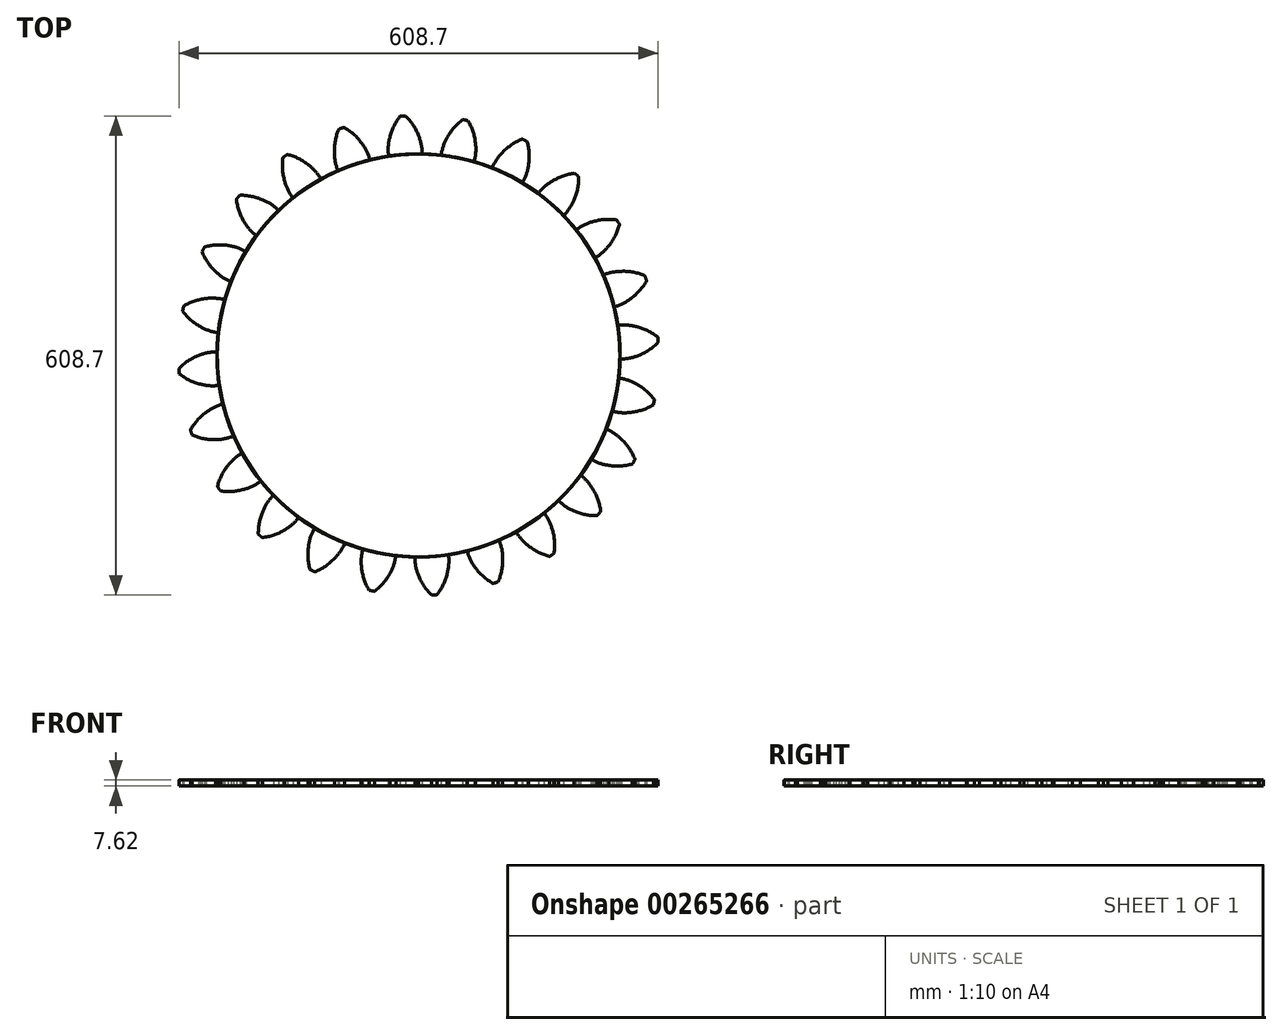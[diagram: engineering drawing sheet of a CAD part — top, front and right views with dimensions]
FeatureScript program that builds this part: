
annotation { "Feature Type Name" : "Feature", "Feature Type Description" : "" }
export const myFeature = defineFeature(function(context is Context, id is Id, definition is map)
    precondition{}
    {
        {
            var Q0;
            Q0=qCreatedBy(makeId("Top.planeOp"),FACE);
            var sketch = newSketch(context, id + "F0", { "sketchPlane" : qUnion([Q0])});
            skCircle(sketch, "E0", {"center": v(0, 0) * mm, "radius": 256.02 * mm});
            skCircle(sketch, "E1", {"center": v(0, 0) * mm, "radius": 279.3 * mm, "construction": true});
            skCircle(sketch, "E2", {"center": v(0, 0) * mm, "radius": 304.8 * mm, "construction": true});
            skLineSegment(sketch, "E3", {"start": v(0, 0) * mm, "end": v(0, 420.14) * mm, "construction": true});
            skLineSegment(sketch, "E4", {"start": v(0, 0) * mm, "end": v(-26.71, 407.56) * mm, "construction": true});
            skLineSegment(sketch, "E5", {"start": v(0, 279.3) * mm, "end": v(-381.83, 279.3) * mm, "construction": true});
            skLineSegment(sketch, "E6", {"start": v(0, 279.3) * mm, "end": v(-397.99, 134.44) * mm, "construction": true});
            skCircle(sketch, "E7", {"center": v(0, 0) * mm, "radius": 262.45 * mm, "construction": true});
            skCircle(sketch, "E8", {"center": v(0, 279.3) * mm, "radius": 69.82 * mm, "construction": true});
            skCircle(sketch, "E9", {"center": v(-65.17, 254.23) * mm, "radius": 69.82 * mm, "construction": true});
            skArc(sketch, "E10", {"start": v(-16.55, 304.35) * mm, "mid": v(-19.94, 304.2) * mm, "end": v(-23.32, 303.9) * mm});
            skArc(sketch, "E11", {"start": v(0, 279.3) * mm, "mid": v(-6.88, 292.75) * mm, "end": v(-16.55, 304.35) * mm});
            skArc(sketch, "E12.MirrorCS", {"start": v(-36.46, 276.9) * mm, "mid": v(-31.4, 291.14) * mm, "end": v(-23.32, 303.9) * mm});
            skArc(sketch, "E13", {"start": v(-36.46, 276.9) * mm, "mid": v(-38.45, 265.13) * mm, "end": v(-38, 253.19) * mm});
            skArc(sketch, "E14.MirrorCS", {"start": v(0, 279.3) * mm, "mid": v(3.51, 267.88) * mm, "end": v(4.63, 255.98) * mm});
            skSolve(sketch);
        }
        {
            var Q0;
            Q0 = qSketchRegion(id + "F0", true);
            extrude(context, id + "F1", {"entities" : qUnion([Q0]), "depth" : 7.62 * mm});
        }
        {
            var Q0;
            Q0=makeQuery(id+"F1.opExtrude","SWEPT_BODY",BODY,{"disambiguationData":[OSD([sQuery(id+"F0.wireOp",EDGE,"E0"),sQuery(id+"F0.wireOp",EDGE,"91NiUCr4-yXFt-oEsC-2t8w-iLQuIMEs0WGp"),sQuery(id+"F0.wireOp",EDGE,"2eccd6a7-b62e-4e30-96b3-c5b5e07e5a5b0.MirrorCS"),sQuery(id+"F0.wireOp",EDGE,"E10")])]});
            var Q1;
            Q1=makeQuery(id+"F1.opExtrude","SWEPT_FACE",FACE,{"disambiguationData":[OSD([sQuery(id+"F0.wireOp",EDGE,"E0")])]});
            circularPattern(context, id + "F2", {"entities" : qUnion([Q0]), "axis" : qUnion([Q1]), "angle" : 360 * degree, "instanceCount" : 24, "equalSpace" : true});
        }
    });
